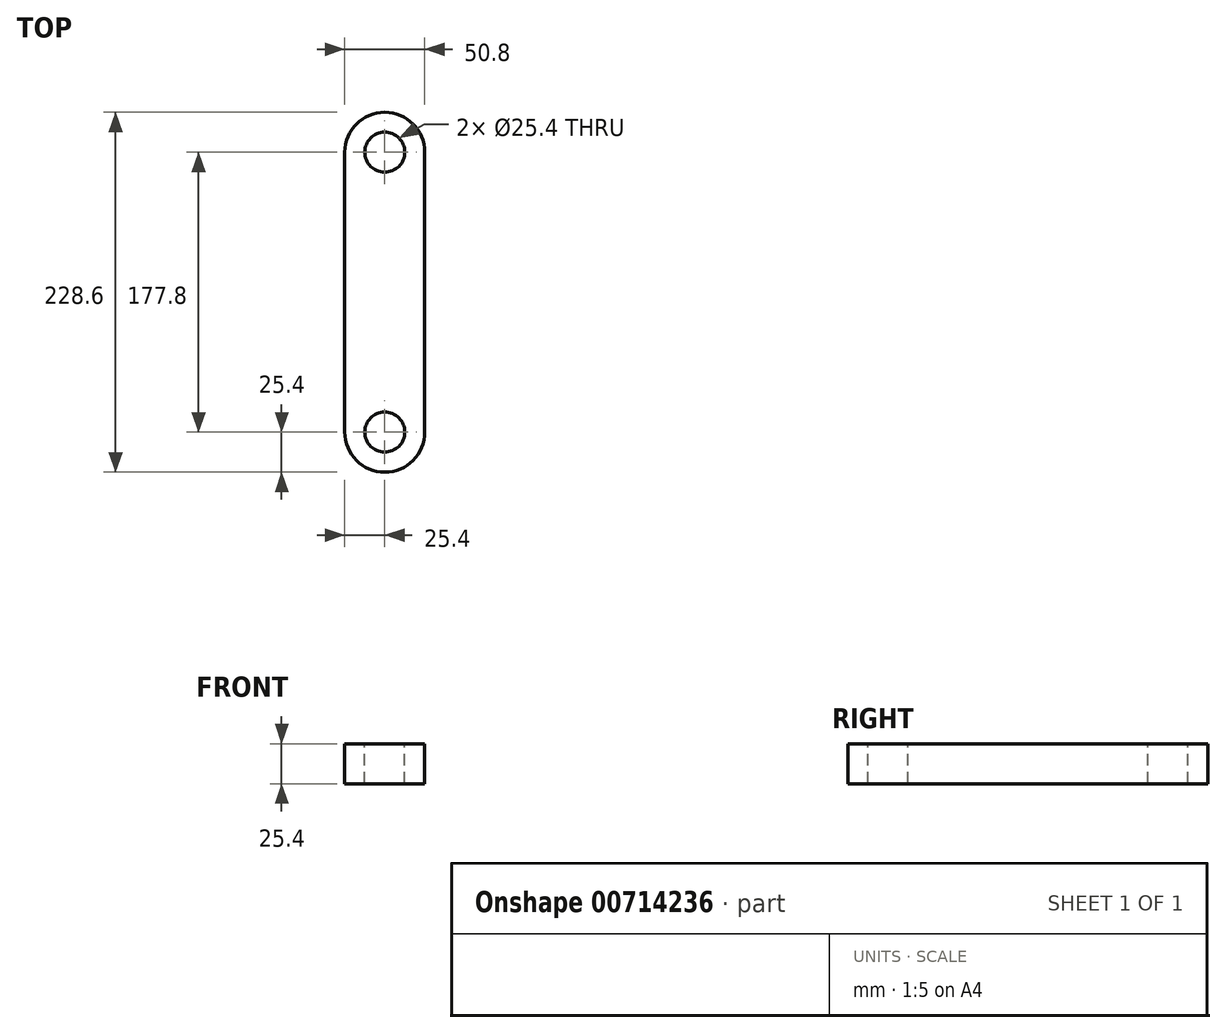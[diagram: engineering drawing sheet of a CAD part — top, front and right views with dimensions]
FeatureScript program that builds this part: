
annotation { "Feature Type Name" : "Feature", "Feature Type Description" : "" }
export const myFeature = defineFeature(function(context is Context, id is Id, definition is map)
    precondition{}
    {
        {
            var Q0;
            Q0=qCreatedBy(makeId("Top.planeOp"),FACE);
            var sketch = newSketch(context, id + "F0", { "sketchPlane" : qUnion([Q0])});
            skLineSegment(sketch, "E0.bottom", {"start": v(-25.4, 0) * mm, "end": v(25.4, 0) * mm});
            skLineSegment(sketch, "E0.top", {"start": v(-25.4, 88.9) * mm, "end": v(25.4, 88.9) * mm});
            skLineSegment(sketch, "E0.left", {"start": v(-25.4, 0) * mm, "end": v(-25.4, 88.9) * mm});
            skLineSegment(sketch, "E0.right", {"start": v(25.4, 0) * mm, "end": v(25.4, 88.9) * mm});
            skCircle(sketch, "E1", {"center": v(0, 88.9) * mm, "radius": 25.4 * mm});
            skSolve(sketch);
        }
        {
            var Q0;
            Q0 = qSketchRegion(id + "F0", true);
            extrude(context, id + "F1", {"entities" : qUnion([Q0]), "depth" : 25.4 * mm, "offsetDistance" : 25.4 * mm});
        }
        {
            var Q0;
            Q0=makeQuery(id+"F1.opExtrude","CAP_FACE",FACE,{"disambiguationData":[OSD([sQuery(id+"F0.wireOp",EDGE,"E0.bottom"),sQuery(id+"F0.wireOp",EDGE,"E0.left"),sQuery(id+"F0.wireOp",EDGE,"E0.right"),sQuery(id+"F0.wireOp",EDGE,"E1")])],"isStart":false});
            var sketch = newSketch(context, id + "F2", { "sketchPlane" : qUnion([Q0])});
            skCircle(sketch, "E2", {"center": v(0, 88.9) * mm, "radius": 12.7 * mm});
            skSolve(sketch);
        }
        {
            var Q0;
            Q0=makeQuery(id+"F2.imprint","IMPRINT",FACE,{"disambiguationData":[TD([[makeQuery(id+"F2.imprint","IMPRINT",EDGE,{"derivedFrom":sQuery(id+"F2.wireOp",EDGE,"E2")}),1.0]])]});
            extrude(context, id + "F3", {"entities" : qUnion([Q0]), "operationType" : NewBodyOperationType.REMOVE, "oppositeDirection" : true, "depth" : 25.4 * mm, "offsetDistance" : 25.4 * mm});
        }
        {
            var Q0;
            Q0=makeQuery(id+"F1.opExtrude","SWEPT_BODY",BODY,{"disambiguationData":[OSD([sQuery(id+"F0.wireOp",EDGE,"E0.bottom"),sQuery(id+"F0.wireOp",EDGE,"E0.left"),sQuery(id+"F0.wireOp",EDGE,"E0.right"),sQuery(id+"F0.wireOp",EDGE,"E1")])]});
            var Q1;
            Q1=makeQuery(id+"F1.opExtrude","SWEPT_FACE",FACE,{"disambiguationData":[OSD([sQuery(id+"F0.wireOp",EDGE,"E0.bottom")])]});
            mirror(context, id + "F4", {"operationType" : NewBodyOperationType.ADD, "entities" : qUnion([Q0]), "mirrorPlane" : qUnion([Q1])});
        }
    });
